# Revit family: DORMA TS 90 IMPULS
name_source: partatom
category: Specialty Equipment
revit_build: Autodesk Revit 2016 (Build: 20150220_1215(x64)
units: mm (PartAtom-declared; Revit-internal decimal feet)

## family parameters
Always vertical = Yes
Cut with Voids When Loaded = Yes
OmniClass Number = 23.30.10.11
OmniClass Title = Door Components
Part Type = Normal
Room Calculation Point = No
Round Connector Dimension = Use Diameter
Shared = Yes
Work Plane-Based = No

## types (5) — shared parameters
BTS 75 Length = 308 mm
BTS 75 width = 105 mm
BTS 80 length = 358 mm
BTS 80 width = 105 mm
Manufacturer = DORMA
URL = http://www.dorma-uk.co.uk

## per-type parameters (varying)
| type | Description | Model |
| BTS 75 | DORMA TS 93 Door closer | TS 93 EN 2-5 |
| TS 93 | DORMA TS 91 Door closer | TS 91 EN 3 |
| TS 91 | DORMA TS 92 Door closer | TS 92 EN 2-4 |
| TS 92 | DORMA TS 90 impulse Door closer | TS 90 |
| TS 90 | DORMA TS 90 impulse Door closer | TS 90 |

## geometry (parser evidence)
native form markers: Blend x6, Sweep x2
no freeform markers — native parametric forms only
